# Revit family: FP-Revit19-en-OS60NDTDX1-WallOven-0-90004673A-CN_CLEARANCES REQUIRED REVISED
name_source: partatom
category: Specialty Equipment
units: mm (PartAtom-declared; Revit-internal decimal feet)

## family parameters
Always vertical = No
Cut with Voids When Loaded = No
Part Type = Normal
Room Calculation Point = No
Round Connector Dimension = Use Diameter
Shared = No
Work Plane-Based = No

## types (1)
- OS60NDTDX1
    Cavity - Depth = 550 mm
    Cavity - Height = 440 mm  [stored 1.44357 ft]
    Cavity - Width = 560 mm  [stored 1.83727 ft]
    Chassis = Fisher & Paykel - Steel Galvanized
    Chassis - Depth = 545 mm  [stored 1.78806 ft]
    Chassis - Height = 435 mm  [stored 1.42717 ft]
    Chassis - Width = 556 mm  [stored 1.82415 ft]
    Clearance = 2 mm  [stored 0.00656168 ft]
    Control Panel = Fisher & Paykel - Glass, Black
    Control Panel - Depth = 20 mm  [stored 0.0656168 ft]
    Default Elevation = 0 mm  [stored 0 ft]
    Description = Compact Steam Oven, 60cm
    Dial = Fisher & Paykel - Aluminium
    Door = Fisher & Paykel - Glass, Black
    Electrical Connection = 220-240V, 50Hz ,15A
    FFL Offset (default) = 900 mm  [stored 2.95276 ft]
    Handle = Fisher & Paykel - Aluminium
    Handle - Depth = 42 mm  [stored 0.137795 ft]
    Manufacturer = Fisher & Paykel Appliances
    Model = OS60NDTDX1
    Product - Height = 458 mm
    Product - Width = 596 mm  [stored 1.95538 ft]
    Trim = Fisher & Paykel - Aluminium
    URL = www.fisherpaykel.com

note: [stored X ft] marks values corroborated as IEEE doubles in the binary element streams (Revit-internal decimal feet)

## geometry (parser evidence)
native form markers: Sweep x3
no freeform markers — native parametric forms only
